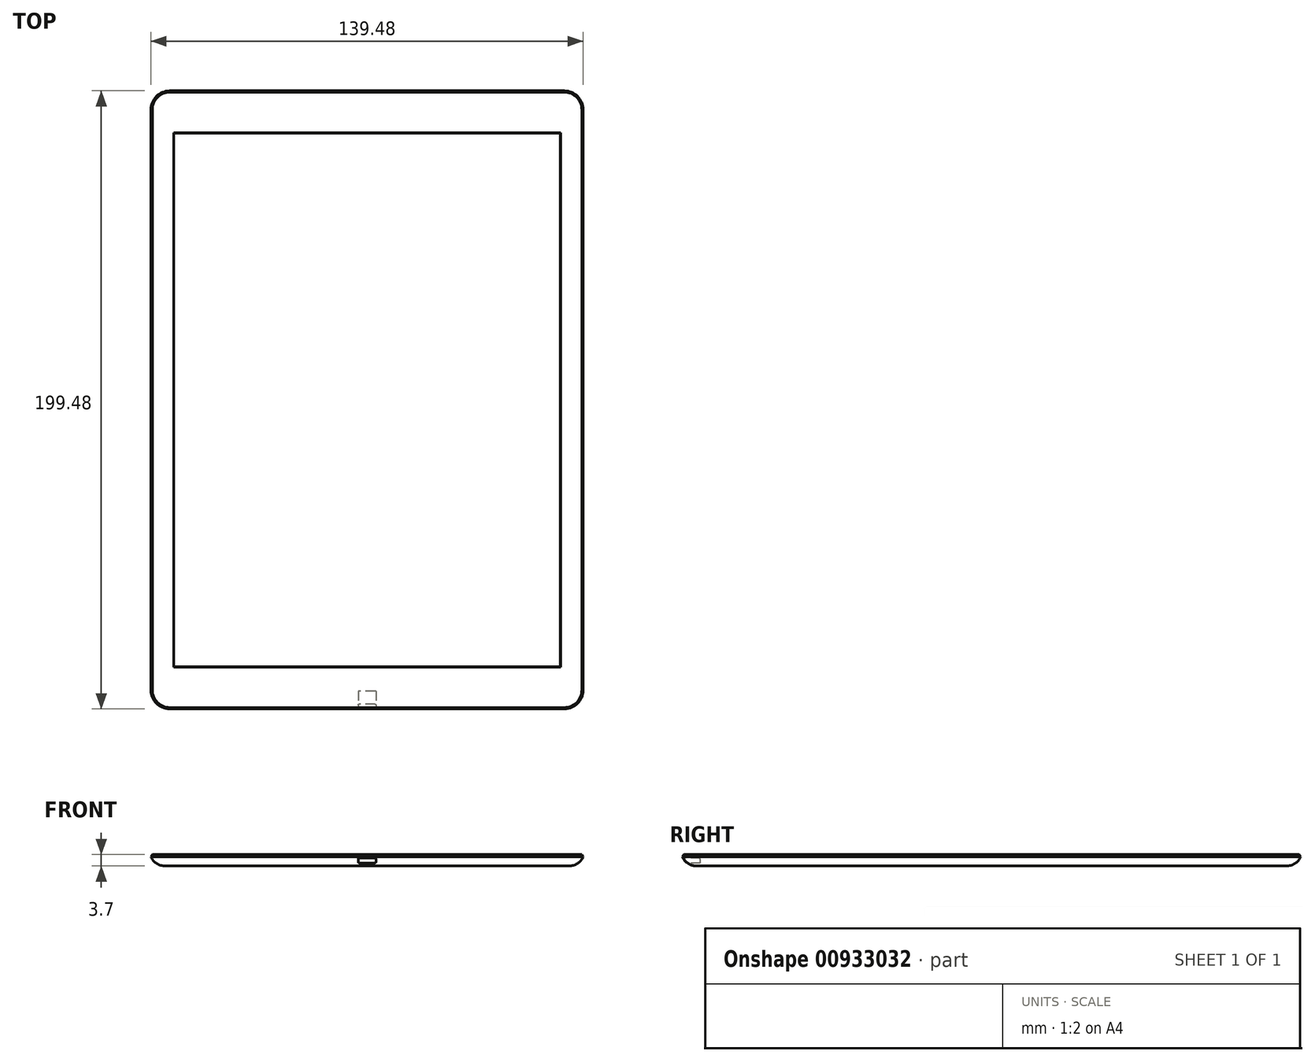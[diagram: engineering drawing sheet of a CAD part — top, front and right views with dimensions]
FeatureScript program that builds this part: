
annotation { "Feature Type Name" : "Feature", "Feature Type Description" : "" }
export const myFeature = defineFeature(function(context is Context, id is Id, definition is map)
    precondition{}
    {
        {
            var Q0;
            Q0=qCreatedBy(makeId("Top.planeOp"),FACE);
            var sketch = newSketch(context, id + "F0", { "sketchPlane" : qUnion([Q0])});
            skLineSegment(sketch, "E0.bottom", {"start": v(63.65, -100) * mm, "end": v(-63.65, -100) * mm});
            skLineSegment(sketch, "E0.top", {"start": v(63.65, 100) * mm, "end": v(-63.65, 100) * mm});
            skLineSegment(sketch, "E0.left", {"start": v(70, -93.65) * mm, "end": v(70, 93.65) * mm});
            skLineSegment(sketch, "E0.right", {"start": v(-70, -93.65) * mm, "end": v(-70, 93.65) * mm});
            skPoint(sketch, "E0.middle", {"position": v(0, 0) * mm});
            skPoint(sketch, "E1.visualSharp", {"position": v(-70, 100) * mm});
            skArc(sketch, "E1.filletArc", {"start": v(-63.65, 100) * mm, "mid": v(-68.14, 98.14) * mm, "end": v(-70, 93.65) * mm});
            skPoint(sketch, "E2.visualSharp", {"position": v(-70, -100) * mm});
            skArc(sketch, "E2.filletArc", {"start": v(-70, -93.65) * mm, "mid": v(-68.14, -98.14) * mm, "end": v(-63.65, -100) * mm});
            skPoint(sketch, "E3.visualSharp", {"position": v(70, -100) * mm});
            skArc(sketch, "E3.filletArc", {"start": v(63.65, -100) * mm, "mid": v(68.14, -98.14) * mm, "end": v(70, -93.65) * mm});
            skPoint(sketch, "E4.visualSharp", {"position": v(70, 100) * mm});
            skArc(sketch, "E4.filletArc", {"start": v(70, 93.65) * mm, "mid": v(68.14, 98.14) * mm, "end": v(63.65, 100) * mm});
            skSolve(sketch);
        }
        {
            var Q0;
            Q0=makeQuery(id+"F0.imprint","IMPRINT",FACE,{"disambiguationData":[TD([[makeQuery(id+"F0.imprint","IMPRINT",EDGE,{"derivedFrom":sQuery(id+"F0.wireOp",EDGE,"E0.bottom")}),-1.0]])]});
            extrude(context, id + "F1", {"entities" : qUnion([Q0]), "depth" : 3.7 * mm, "offsetDistance" : 25.4 * mm});
        }
        {
            var Q0;
            Q0=makeQuery(id+"F1.opExtrude","SWEPT_FACE",FACE,{"disambiguationData":[OSD([sQuery(id+"F0.wireOp",EDGE,"E0.bottom")])]});
            var sketch = newSketch(context, id + "F2", { "sketchPlane" : qUnion([Q0])});
            skLineSegment(sketch, "E5.bottom", {"start": v(2.53, 2.6) * mm, "end": v(-2.53, 2.6) * mm});
            skLineSegment(sketch, "E5.top", {"start": v(2.53, 1) * mm, "end": v(-2.53, 1) * mm});
            skLineSegment(sketch, "E5.left", {"start": v(2.86, 2.26) * mm, "end": v(2.86, 1.33) * mm});
            skLineSegment(sketch, "E5.right", {"start": v(-2.86, 2.26) * mm, "end": v(-2.86, 1.33) * mm});
            skPoint(sketch, "E5.middle", {"position": v(0, 1.8) * mm});
            skPoint(sketch, "E5.middle.positionSnap0", {"position": v(0, 3.7) * mm});
            skPoint(sketch, "E5.centerSnap0", {"position": v(0, 3.7) * mm});
            skPoint(sketch, "E6.visualSharp", {"position": v(2.86, 2.6) * mm});
            skArc(sketch, "E6.filletArc", {"start": v(2.86, 2.26) * mm, "mid": v(2.76, 2.5) * mm, "end": v(2.53, 2.6) * mm});
            skPoint(sketch, "E7.visualSharp", {"position": v(2.86, 1) * mm});
            skArc(sketch, "E7.filletArc", {"start": v(2.53, 1) * mm, "mid": v(2.76, 1.1) * mm, "end": v(2.86, 1.33) * mm});
            skPoint(sketch, "E8.visualSharp", {"position": v(-2.86, 2.6) * mm});
            skArc(sketch, "E8.filletArc", {"start": v(-2.53, 2.6) * mm, "mid": v(-2.76, 2.5) * mm, "end": v(-2.86, 2.26) * mm});
            skPoint(sketch, "E9.visualSharp", {"position": v(-2.86, 1) * mm});
            skArc(sketch, "E9.filletArc", {"start": v(-2.86, 1.33) * mm, "mid": v(-2.76, 1.1) * mm, "end": v(-2.53, 1) * mm});
            skSolve(sketch);
        }
        {
            var Q0;
            Q0=makeQuery(id+"F2.imprint","IMPRINT",FACE,{"disambiguationData":[TD([[makeQuery(id+"F2.imprint","IMPRINT",EDGE,{"derivedFrom":sQuery(id+"F2.wireOp",EDGE,"E5.bottom")}),1.0]])]});
            extrude(context, id + "F3", {"entities" : qUnion([Q0]), "operationType" : NewBodyOperationType.REMOVE, "oppositeDirection" : true, "depth" : 6 * mm, "offsetDistance" : 25.4 * mm});
        }
        {
            var Q0;
            Q0=makeQuery(id+"F1.opExtrude","CAP_FACE",FACE,{"disambiguationData":[OSD([sQuery(id+"F0.wireOp",EDGE,"E0.bottom"),sQuery(id+"F0.wireOp",EDGE,"E0.top"),sQuery(id+"F0.wireOp",EDGE,"E0.left"),sQuery(id+"F0.wireOp",EDGE,"E0.right")])],"isStart":false});
            var sketch = newSketch(context, id + "F4", { "sketchPlane" : qUnion([Q0])});
            skLineSegment(sketch, "E10.bottom", {"start": v(61.93, -85.73) * mm, "end": v(-61.93, -85.73) * mm});
            skLineSegment(sketch, "E10.top", {"start": v(61.93, 85.73) * mm, "end": v(-61.93, 85.73) * mm});
            skLineSegment(sketch, "E10.left", {"start": v(61.93, -85.73) * mm, "end": v(61.93, 85.73) * mm});
            skLineSegment(sketch, "E10.right", {"start": v(-61.93, -85.73) * mm, "end": v(-61.93, 85.73) * mm});
            skPoint(sketch, "E10.middle", {"position": v(0, 0) * mm});
            skSolve(sketch);
        }
        {
            var Q0;
            Q0=makeQuery(id+"F4.imprint","IMPRINT",FACE,{"disambiguationData":[TD([[makeQuery(id+"F4.imprint","IMPRINT",EDGE,{"derivedFrom":sQuery(id+"F4.wireOp",EDGE,"E10.bottom")}),-1.0]])]});
            extrude(context, id + "F5", {"entities" : qUnion([Q0]), "operationType" : NewBodyOperationType.REMOVE, "oppositeDirection" : true, "depth" : 0.1 * mm, "offsetDistance" : 25.4 * mm});
        }
        {
            var Q0;
            Q0=makeQuery(id+"F1.opExtrude","CAP_FACE",FACE,{"disambiguationData":[OSD([sQuery(id+"F0.wireOp",EDGE,"E0.bottom"),sQuery(id+"F0.wireOp",EDGE,"E0.top"),sQuery(id+"F0.wireOp",EDGE,"E0.left"),sQuery(id+"F0.wireOp",EDGE,"E0.right")])],"isStart":false});
            var sketch = newSketch(context, id + "F6", { "sketchPlane" : qUnion([Q0])});
            skCircle(sketch, "E11", {"center": v(0, -93.08) * mm, "radius": 4.78 * mm});
            skSolve(sketch);
        }
        {
            var Q0;
            Q0=makeQuery(id+"F6.imprint","IMPRINT",FACE,{"disambiguationData":[TD([[makeQuery(id+"F6.imprint","IMPRINT",EDGE,{"derivedFrom":sQuery(id+"F6.wireOp",EDGE,"E11")}),1.0]])]});
            extrude(context, id + "F7", {"entities" : qUnion([Q0]), "operationType" : NewBodyOperationType.REMOVE, "oppositeDirection" : true, "depth" : 0.5 * mm, "offsetDistance" : 25.4 * mm});
        }
        {
            var Q0;
            Q0=makeQuery(id+"F7.boolean.opBoolean","COPY",EDGE,{"derivedFrom":makeQuery(id+"F7.opExtrude","CAP_EDGE",EDGE,{"disambiguationData":[OSD([sQuery(id+"F6.wireOp",EDGE,"E11")])],"isStart":false})});
            fillet(context, id + "F8", {"entities" : qUnion([Q0]), "radius" : 2 * mm, "tangentPropagation" : true, "allowEdgeOverflow" : false});
        }
        {
            var Q0;
            Q0=makeQuery(id+"F8.opFillet","BLEND_EDGE",EDGE,{"blendedFrom":[makeQuery(id+"F7.boolean.opBoolean","COPY",EDGE,{"derivedFrom":makeQuery(id+"F7.opExtrude","CAP_EDGE",EDGE,{"disambiguationData":[OSD([sQuery(id+"F6.wireOp",EDGE,"E11")])],"isStart":false})}),makeQuery(id+"F1.opExtrude","CAP_FACE",FACE,{"disambiguationData":[OSD([sQuery(id+"F0.wireOp",EDGE,"E0.bottom"),sQuery(id+"F0.wireOp",EDGE,"E0.top"),sQuery(id+"F0.wireOp",EDGE,"E0.left"),sQuery(id+"F0.wireOp",EDGE,"E0.right")])],"isStart":false})],"blendedInto":[makeQuery(id+"F1.opExtrude","CAP_FACE",FACE,{"disambiguationData":[OSD([sQuery(id+"F0.wireOp",EDGE,"E0.bottom"),sQuery(id+"F0.wireOp",EDGE,"E0.top"),sQuery(id+"F0.wireOp",EDGE,"E0.left"),sQuery(id+"F0.wireOp",EDGE,"E0.right")])],"isStart":false})]});
            fillet(context, id + "F9", {"entities" : qUnion([Q0]), "radius" : 1 * mm, "tangentPropagation" : true, "allowEdgeOverflow" : false});
        }
        {
            var Q0;
            Q0=makeQuery(id+"F1.opExtrude","CAP_FACE",FACE,{"disambiguationData":[OSD([sQuery(id+"F0.wireOp",EDGE,"E0.bottom"),sQuery(id+"F0.wireOp",EDGE,"E0.top"),sQuery(id+"F0.wireOp",EDGE,"E0.left"),sQuery(id+"F0.wireOp",EDGE,"E0.right")])],"isStart":true});
            fillet(context, id + "F10", {"entities" : qUnion([Q0]), "radius" : 5.08 * mm, "tangentPropagation" : true, "allowEdgeOverflow" : false});
        }
        {
            var Q0;
            Q0=makeQuery(id+"F1.opExtrude","CAP_FACE",FACE,{"disambiguationData":[OSD([sQuery(id+"F0.wireOp",EDGE,"E0.bottom"),sQuery(id+"F0.wireOp",EDGE,"E0.top"),sQuery(id+"F0.wireOp",EDGE,"E0.left"),sQuery(id+"F0.wireOp",EDGE,"E0.right")])],"isStart":false});
            var Q1;
            Q1=makeQuery(id+"F10.opFillet","BLEND_FACE",FACE,{"disambiguationData":[OSD([sQuery(id+"F0.wireOp",EDGE,"E0.right")])]});
            chamfer(context, id + "F11", {"entities" : qUnion([Q0, Q1]), "width" : 0.5 * mm, "tangentPropagation" : true});
        }
    });
